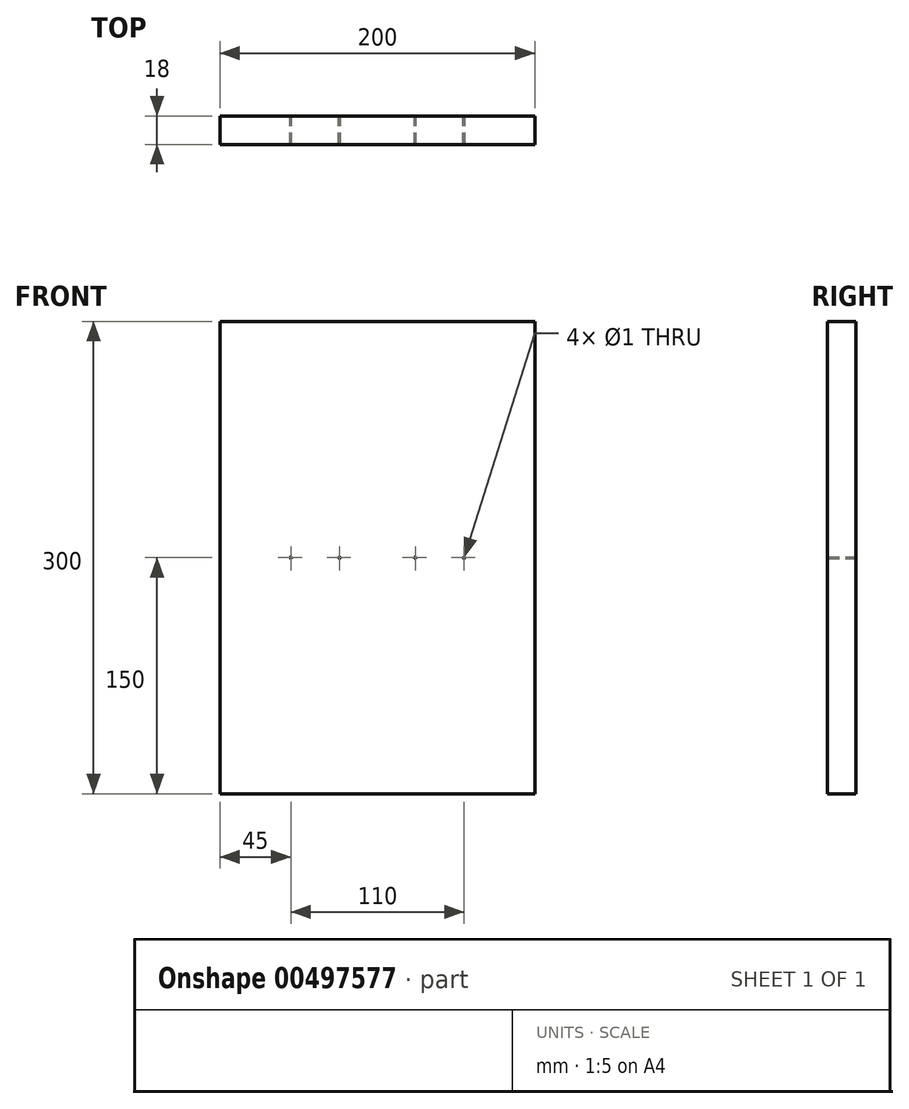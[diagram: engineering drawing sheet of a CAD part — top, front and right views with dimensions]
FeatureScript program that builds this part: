
annotation { "Feature Type Name" : "Feature", "Feature Type Description" : "" }
export const myFeature = defineFeature(function(context is Context, id is Id, definition is map)
    precondition{}
    {
        {
            var Q0;
            Q0=qCreatedBy(makeId("Front.planeOp"),FACE);
            var sketch = newSketch(context, id + "F0", { "sketchPlane" : qUnion([Q0])});
            skLineSegment(sketch, "E0.bottom", {"start": v(0, 0) * mm, "end": v(200, 0) * mm});
            skLineSegment(sketch, "E0.top", {"start": v(0, 300) * mm, "end": v(200, 300) * mm});
            skLineSegment(sketch, "E0.left", {"start": v(0, 0) * mm, "end": v(0, 300) * mm});
            skLineSegment(sketch, "E0.right", {"start": v(200, 0) * mm, "end": v(200, 300) * mm});
            skPoint(sketch, "E1.centerSnap0", {"position": v(200, 150) * mm});
            skLineSegment(sketch, "E2", {"start": v(100, 300) * mm, "end": v(100, 0) * mm, "construction": true});
            skCircle(sketch, "E3", {"center": v(45, 150) * mm, "radius": 0.5 * mm});
            skPoint(sketch, "E3.centerSnap0", {"position": v(100, 150) * mm});
            skCircle(sketch, "E4.MirrorC", {"center": v(155, 150) * mm, "radius": 0.5 * mm});
            skCircle(sketch, "E5", {"center": v(124.05, 150) * mm, "radius": 0.5 * mm});
            skCircle(sketch, "E6.MirrorC", {"center": v(75.95, 150) * mm, "radius": 0.5 * mm});
            skSolve(sketch);
        }
        {
            var Q0;
            Q0=makeQuery(id+"F0.imprint","IMPRINT",FACE,{"disambiguationData":[TD([[makeQuery(id+"F0.imprint","IMPRINT",EDGE,{"derivedFrom":sQuery(id+"F0.wireOp",EDGE,"E0.bottom")}),1.0]])]});
            extrude(context, id + "F1", {"entities" : qUnion([Q0]), "depth" : 18 * mm, "offsetDistance" : 25.4 * mm});
        }
    });
